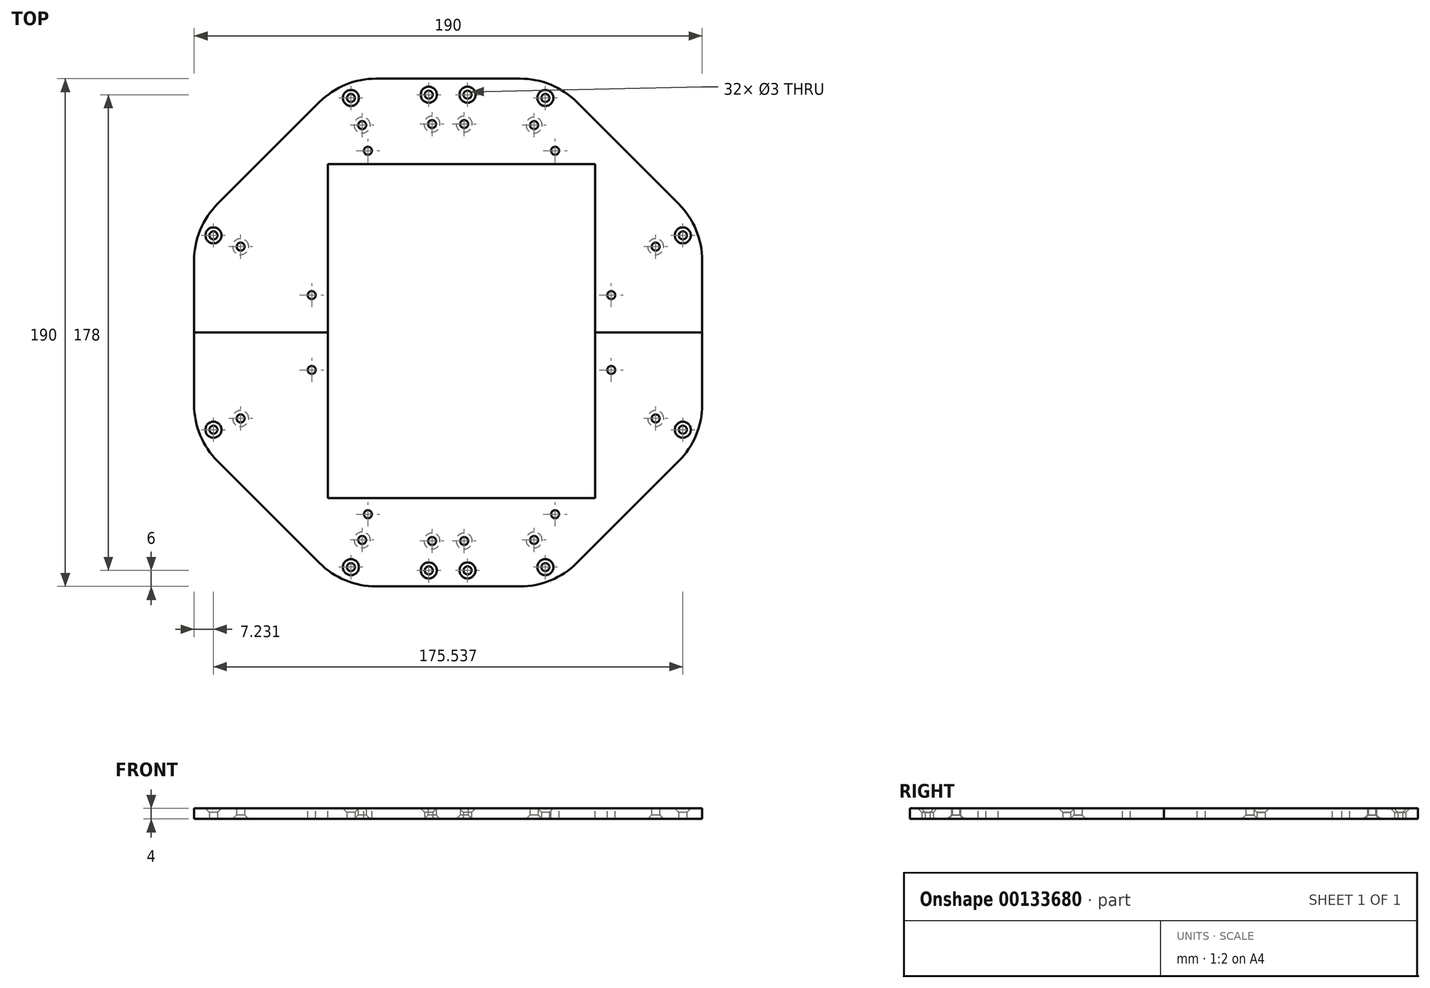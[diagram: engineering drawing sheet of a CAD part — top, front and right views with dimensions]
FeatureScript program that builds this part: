
annotation { "Feature Type Name" : "Feature", "Feature Type Description" : "" }
export const myFeature = defineFeature(function(context is Context, id is Id, definition is map)
    precondition{}
    {
        {
            var Q0;
            Q0=qCreatedBy(makeId("Top.planeOp"),FACE);
            var sketch = newSketch(context, id + "F0", { "sketchPlane" : qUnion([Q0])});
            skCircle(sketch, "E0.cCircle", {"center": v(0, 0) * mm, "radius": 95 * mm, "construction": true});
            skLineSegment(sketch, "E0.0", {"start": v(39.35, -95) * mm, "end": v(-39.35, -95) * mm});
            skLineSegment(sketch, "E0.1", {"start": v(-39.35, -95) * mm, "end": v(-95, -39.35) * mm});
            skLineSegment(sketch, "E0.2", {"start": v(-95, -39.35) * mm, "end": v(-95, 39.35) * mm});
            skLineSegment(sketch, "E0.3", {"start": v(-95, 39.35) * mm, "end": v(-39.35, 95) * mm});
            skLineSegment(sketch, "E0.4", {"start": v(-39.35, 95) * mm, "end": v(39.35, 95) * mm});
            skLineSegment(sketch, "E0.5", {"start": v(39.35, 95) * mm, "end": v(95, 39.35) * mm});
            skLineSegment(sketch, "E0.6", {"start": v(95, 39.35) * mm, "end": v(95, -39.35) * mm});
            skLineSegment(sketch, "E0.7", {"start": v(95, -39.35) * mm, "end": v(39.35, -95) * mm});
            skLineSegment(sketch, "E1", {"start": v(0, 0) * mm, "end": v(-95, 0) * mm});
            skLineSegment(sketch, "E2", {"start": v(0, 0) * mm, "end": v(95, 0) * mm});
            skLineSegment(sketch, "E3", {"start": v(-95, -39.35) * mm, "end": v(0, 0) * mm, "construction": true});
            skCircle(sketch, "E4", {"center": v(-87.77, -36.35) * mm, "radius": 1.5 * mm});
            skCircle(sketch, "E5.1.0", {"center": v(-36.35, -87.77) * mm, "radius": 1.5 * mm});
            skCircle(sketch, "E5.2.0", {"center": v(36.35, -87.77) * mm, "radius": 1.5 * mm});
            skCircle(sketch, "E5.3.0", {"center": v(87.77, -36.35) * mm, "radius": 1.5 * mm});
            skCircle(sketch, "E5.4.0", {"center": v(87.77, 36.35) * mm, "radius": 1.5 * mm});
            skCircle(sketch, "E5.5.0", {"center": v(36.35, 87.77) * mm, "radius": 1.5 * mm});
            skCircle(sketch, "E5.6.0", {"center": v(-36.35, 87.77) * mm, "radius": 1.5 * mm});
            skCircle(sketch, "E5.7.0", {"center": v(-87.77, 36.35) * mm, "radius": 1.5 * mm});
            skCircle(sketch, "E6", {"center": v(-77.6, -32.15) * mm, "radius": 1.5 * mm});
            skLineSegment(sketch, "E7", {"start": v(0, 0) * mm, "end": v(0, -89) * mm, "construction": true});
            skLineSegment(sketch, "E8", {"start": v(0, -89) * mm, "end": v(-7.25, -89) * mm, "construction": true});
            skLineSegment(sketch, "E9", {"start": v(0, -89) * mm, "end": v(7.25, -89) * mm, "construction": true});
            skCircle(sketch, "E10", {"center": v(-7.25, -89) * mm, "radius": 1.5 * mm});
            skCircle(sketch, "E11", {"center": v(7.25, -89) * mm, "radius": 1.5 * mm});
            skCircle(sketch, "E12.1.0", {"center": v(7.25, 89) * mm, "radius": 1.5 * mm});
            skCircle(sketch, "E12.1.1", {"center": v(-7.25, 89) * mm, "radius": 1.5 * mm});
            skCircle(sketch, "E13.1.0", {"center": v(-32.15, -77.6) * mm, "radius": 1.5 * mm});
            skCircle(sketch, "E13.2.0", {"center": v(32.15, -77.6) * mm, "radius": 1.5 * mm});
            skCircle(sketch, "E13.3.0", {"center": v(77.6, -32.15) * mm, "radius": 1.5 * mm});
            skCircle(sketch, "E13.4.0", {"center": v(77.6, 32.15) * mm, "radius": 1.5 * mm});
            skCircle(sketch, "E13.5.0", {"center": v(32.15, 77.6) * mm, "radius": 1.5 * mm});
            skCircle(sketch, "E13.6.0", {"center": v(-32.15, 77.6) * mm, "radius": 1.5 * mm});
            skCircle(sketch, "E13.7.0", {"center": v(-77.6, 32.15) * mm, "radius": 1.5 * mm});
            skLineSegment(sketch, "E14", {"start": v(0, -78) * mm, "end": v(-6, -78) * mm, "construction": true});
            skLineSegment(sketch, "E15", {"start": v(0, -78) * mm, "end": v(6, -78) * mm, "construction": true});
            skCircle(sketch, "E16", {"center": v(-6, -78) * mm, "radius": 1.5 * mm});
            skCircle(sketch, "E17", {"center": v(6, -78) * mm, "radius": 1.5 * mm});
            skCircle(sketch, "E18.1.0", {"center": v(-6, 78) * mm, "radius": 1.5 * mm});
            skCircle(sketch, "E18.1.1", {"center": v(6, 78) * mm, "radius": 1.5 * mm});
            skSolve(sketch);
        }
        {
            var Q0;
            {var subQ1=sQuery(id+"F0.wireOp",EDGE,"E0.3");Q0=makeQuery(id+"F0.imprint","IMPRINT",FACE,{"disambiguationData":[TD([[makeQuery(id+"F0.imprint","IMPRINT",EDGE,{"derivedFrom":subQ1}),-1.0]])]});}
            var Q1;
            {var subQ1=sQuery(id+"F0.wireOp",EDGE,"E0.3");Q1=makeQuery(id+"F0.imprint","IMPRINT",FACE,{"disambiguationData":[TD([[makeQuery(id+"F0.imprint","IMPRINT",EDGE,{"derivedFrom":subQ1}),-1.0]])]});}
            extrude(context, id + "F1", {"entities" : qUnion([Q0, Q1]), "depth" : 4 * mm});
        }
        {
            var Q0;
            Q0=makeQuery(id+"F0.imprint","IMPRINT",FACE,{"disambiguationData":[TD([[makeQuery(id+"F0.imprint","IMPRINT",EDGE,{"derivedFrom":sQuery(id+"F0.wireOp",EDGE,"E0.0")}),-1.0]])]});
            extrude(context, id + "F2", {"entities" : qUnion([Q0]), "depth" : 4 * mm});
        }
        {
            var Q0;
            Q0=makeQuery(id+"F2.opExtrude","SWEPT_EDGE",EDGE,{"disambiguationData":[OSD([sQuery(id+"F0.wireOp",EDGE,"E0.1"),sQuery(id+"F0.wireOp",EDGE,"E0.2")])]});
            var Q1;
            Q1=makeQuery(id+"F2.opExtrude","SWEPT_EDGE",EDGE,{"disambiguationData":[OSD([sQuery(id+"F0.wireOp",EDGE,"E0.6"),sQuery(id+"F0.wireOp",EDGE,"E0.7")])]});
            var Q2;
            Q2=makeQuery(id+"F1.opExtrude","SWEPT_EDGE",EDGE,{"disambiguationData":[OSD([sQuery(id+"F0.wireOp",EDGE,"E0.5"),sQuery(id+"F0.wireOp",EDGE,"E0.6")])]});
            var Q3;
            Q3=makeQuery(id+"F1.opExtrude","SWEPT_EDGE",EDGE,{"disambiguationData":[OSD([sQuery(id+"F0.wireOp",EDGE,"E0.4"),sQuery(id+"F0.wireOp",EDGE,"E0.5")])]});
            var Q4;
            Q4=makeQuery(id+"F1.opExtrude","SWEPT_EDGE",EDGE,{"disambiguationData":[OSD([sQuery(id+"F0.wireOp",EDGE,"E0.3"),sQuery(id+"F0.wireOp",EDGE,"E0.4")])]});
            var Q5;
            Q5=makeQuery(id+"F1.opExtrude","SWEPT_EDGE",EDGE,{"disambiguationData":[OSD([sQuery(id+"F0.wireOp",EDGE,"E0.2"),sQuery(id+"F0.wireOp",EDGE,"E0.3")])]});
            var Q6;
            Q6=makeQuery(id+"F2.opExtrude","SWEPT_EDGE",EDGE,{"disambiguationData":[OSD([sQuery(id+"F0.wireOp",EDGE,"E0.0"),sQuery(id+"F0.wireOp",EDGE,"E0.1")])]});
            var Q7;
            Q7=makeQuery(id+"F2.opExtrude","SWEPT_EDGE",EDGE,{"disambiguationData":[OSD([sQuery(id+"F0.wireOp",EDGE,"E0.0"),sQuery(id+"F0.wireOp",EDGE,"E0.7")])]});
            fillet(context, id + "F3", {"entities" : qUnion([Q0, Q1, Q2, Q3, Q4, Q5, Q6, Q7]), "radius" : 30 * mm, "tangentPropagation" : true, "allowEdgeOverflow" : false});
        }
        {
            var Q0;
            Q0=makeQuery(id+"F1.opExtrude","CAP_FACE",FACE,{"disambiguationData":[OSD([sQuery(id+"F0.wireOp",EDGE,"E0.2"),sQuery(id+"F0.wireOp",EDGE,"E0.3"),sQuery(id+"F0.wireOp",EDGE,"E0.4"),sQuery(id+"F0.wireOp",EDGE,"E0.5"),sQuery(id+"F0.wireOp",EDGE,"E0.6"),sQuery(id+"F0.wireOp",EDGE,"FWvXgzkW-92Ol-D1nR-HL31-QDwloOWlVPkl"),sQuery(id+"F0.wireOp",EDGE,"KB5lrl97-oh6M-4FKn-tIKZ-oEGIWaDHRA87"),sQuery(id+"F0.wireOp",EDGE,"1a06ab86-549c-4c23-92a1-abe76b86ff2b"),sQuery(id+"F0.wireOp",EDGE,"3b6d9c79-dd86-4e60-94f1-2d74a6fdfb3c.4.1"),sQuery(id+"F0.wireOp",EDGE,"3b6d9c79-dd86-4e60-94f1-2d74a6fdfb3c.5.0"),sQuery(id+"F0.wireOp",EDGE,"3b6d9c79-dd86-4e60-94f1-2d74a6fdfb3c.5.1"),sQuery(id+"F0.wireOp",EDGE,"3b6d9c79-dd86-4e60-94f1-2d74a6fdfb3c.6.0"),sQuery(id+"F0.wireOp",EDGE,"3b6d9c79-dd86-4e60-94f1-2d74a6fdfb3c.6.1"),sQuery(id+"F0.wireOp",EDGE,"3b6d9c79-dd86-4e60-94f1-2d74a6fdfb3c.7.0"),sQuery(id+"F0.wireOp",EDGE,"3b6d9c79-dd86-4e60-94f1-2d74a6fdfb3c.7.1")])],"isStart":false});
            var sketch = newSketch(context, id + "F4", { "sketchPlane" : qUnion([Q0])});
            skLineSegment(sketch, "E19.bottom", {"start": v(-30, 68) * mm, "end": v(40, 68) * mm, "construction": true});
            skLineSegment(sketch, "E19.top", {"start": v(-30, -68) * mm, "end": v(40, -68) * mm, "construction": true});
            skLineSegment(sketch, "E19.left", {"start": v(-30, 68) * mm, "end": v(-30, -68) * mm, "construction": true});
            skLineSegment(sketch, "E19.right", {"start": v(40, 68) * mm, "end": v(40, -68) * mm, "construction": true});
            skPoint(sketch, "E19.middle", {"position": v(0, 0) * mm});
            skCircle(sketch, "E20", {"center": v(-30, 68) * mm, "radius": 1.5 * mm});
            skCircle(sketch, "E21", {"center": v(40, 68) * mm, "radius": 1.5 * mm});
            skCircle(sketch, "E22", {"center": v(40, -68) * mm, "radius": 1.5 * mm});
            skCircle(sketch, "E23", {"center": v(-30, -68) * mm, "radius": 1.5 * mm});
            skPoint(sketch, "E24", {"position": v(5, 0) * mm});
            skPoint(sketch, "E24.positionSnap0", {"position": v(5, 68) * mm});
            skSolve(sketch);
        }
        {
            var Q0;
            Q0=makeQuery(id+"F4.imprint","IMPRINT",FACE,{"disambiguationData":[TD([[makeQuery(id+"F4.imprint","IMPRINT",EDGE,{"derivedFrom":sQuery(id+"F4.wireOp",EDGE,"E20")}),1.0]])]});
            var Q1;
            Q1=makeQuery(id+"F4.imprint","IMPRINT",FACE,{"disambiguationData":[TD([[makeQuery(id+"F4.imprint","IMPRINT",EDGE,{"derivedFrom":sQuery(id+"F4.wireOp",EDGE,"E21")}),1.0]])]});
            var Q2;
            Q2=makeQuery(id+"F4.imprint","IMPRINT",FACE,{"disambiguationData":[TD([[makeQuery(id+"F4.imprint","IMPRINT",EDGE,{"derivedFrom":sQuery(id+"F4.wireOp",EDGE,"E22")}),1.0]])]});
            var Q3;
            Q3=makeQuery(id+"F4.imprint","IMPRINT",FACE,{"disambiguationData":[TD([[makeQuery(id+"F4.imprint","IMPRINT",EDGE,{"derivedFrom":sQuery(id+"F4.wireOp",EDGE,"E23")}),1.0]])]});
            extrude(context, id + "F5", {"entities" : qUnion([Q0, Q1, Q2, Q3]), "operationType" : NewBodyOperationType.REMOVE, "oppositeDirection" : true, "depth" : 25 * mm});
        }
        {
            var Q0;
            Q0=makeQuery(id+"F1.opExtrude","CAP_FACE",FACE,{"disambiguationData":[OSD([sQuery(id+"F0.wireOp",EDGE,"E0.2"),sQuery(id+"F0.wireOp",EDGE,"E0.3"),sQuery(id+"F0.wireOp",EDGE,"E0.4"),sQuery(id+"F0.wireOp",EDGE,"E0.5"),sQuery(id+"F0.wireOp",EDGE,"E0.6"),sQuery(id+"F0.wireOp",EDGE,"FWvXgzkW-92Ol-D1nR-HL31-QDwloOWlVPkl"),sQuery(id+"F0.wireOp",EDGE,"KB5lrl97-oh6M-4FKn-tIKZ-oEGIWaDHRA87"),sQuery(id+"F0.wireOp",EDGE,"ce847c22-4656-4ac6-8dae-eb3496d83a06.7.0"),sQuery(id+"F0.wireOp",EDGE,"ce847c22-4656-4ac6-8dae-eb3496d83a06.7.1"),sQuery(id+"F0.wireOp",EDGE,"2ddf77b3-c7c5-494c-ac41-90231f072106.1.0"),sQuery(id+"F0.wireOp",EDGE,"2ddf77b3-c7c5-494c-ac41-90231f072106.1.1"),sQuery(id+"F0.wireOp",EDGE,"2ddf77b3-c7c5-494c-ac41-90231f072106.1.2"),sQuery(id+"F0.wireOp",EDGE,"2ddf77b3-c7c5-494c-ac41-90231f072106.1.3"),sQuery(id+"F0.wireOp",EDGE,"2ddf77b3-c7c5-494c-ac41-90231f072106.2.0"),sQuery(id+"F0.wireOp",EDGE,"2ddf77b3-c7c5-494c-ac41-90231f072106.2.1"),sQuery(id+"F0.wireOp",EDGE,"2ddf77b3-c7c5-494c-ac41-90231f072106.2.2"),sQuery(id+"F0.wireOp",EDGE,"2ddf77b3-c7c5-494c-ac41-90231f072106.2.3"),sQuery(id+"F0.wireOp",EDGE,"2ddf77b3-c7c5-494c-ac41-90231f072106.3.0"),sQuery(id+"F0.wireOp",EDGE,"2ddf77b3-c7c5-494c-ac41-90231f072106.3.1"),sQuery(id+"F0.wireOp",EDGE,"2ddf77b3-c7c5-494c-ac41-90231f072106.3.2"),sQuery(id+"F0.wireOp",EDGE,"2ddf77b3-c7c5-494c-ac41-90231f072106.3.3"),sQuery(id+"F0.wireOp",EDGE,"2ddf77b3-c7c5-494c-ac41-90231f072106.4.0"),sQuery(id+"F0.wireOp",EDGE,"2ddf77b3-c7c5-494c-ac41-90231f072106.4.1")])],"isStart":false});
            var sketch = newSketch(context, id + "F6", { "sketchPlane" : qUnion([Q0])});
            skLineSegment(sketch, "E25", {"start": v(-45, 63) * mm, "end": v(55, 63) * mm});
            skLineSegment(sketch, "E26", {"start": v(55, 63) * mm, "end": v(55, -62) * mm});
            skLineSegment(sketch, "E27.top", {"start": v(-45, -62) * mm, "end": v(55, -62) * mm});
            skLineSegment(sketch, "E27.left", {"start": v(-45, 63) * mm, "end": v(-45, -62) * mm});
            skLineSegment(sketch, "E28", {"start": v(-30, 68) * mm, "end": v(40, 68) * mm});
            skLineSegment(sketch, "E29", {"start": v(5, 68) * mm, "end": v(5, 63) * mm});
            skLineSegment(sketch, "E30", {"start": v(0, 0) * mm, "end": v(-51, 0) * mm});
            skLineSegment(sketch, "E31", {"start": v(-51, 0) * mm, "end": v(-51, -14) * mm});
            skLineSegment(sketch, "E32", {"start": v(-51, 0) * mm, "end": v(-51, 14) * mm});
            skCircle(sketch, "E33", {"center": v(-51, 14) * mm, "radius": 1.5 * mm});
            skCircle(sketch, "E34", {"center": v(-51, -14) * mm, "radius": 1.5 * mm});
            skLineSegment(sketch, "E35", {"start": v(0, 0) * mm, "end": v(61, 0) * mm});
            skLineSegment(sketch, "E36", {"start": v(61, 0) * mm, "end": v(61, 14) * mm});
            skLineSegment(sketch, "E37", {"start": v(61, 0) * mm, "end": v(61, -14) * mm});
            skCircle(sketch, "E38", {"center": v(61, 14) * mm, "radius": 1.5 * mm});
            skCircle(sketch, "E39", {"center": v(61, -14) * mm, "radius": 1.5 * mm});
            skLineSegment(sketch, "E40", {"start": v(61, 0) * mm, "end": v(0, 0) * mm});
            skSolve(sketch);
        }
        {
            var Q0;
            Q0=makeQuery(id+"F6.imprint","IMPRINT",FACE,{"disambiguationData":[TD([[makeQuery(id+"F6.imprint","IMPRINT",EDGE,{"derivedFrom":sQuery(id+"F6.wireOp",EDGE,"E33")}),1.0]])]});
            var Q1;
            Q1=makeQuery(id+"F6.imprint","IMPRINT",FACE,{"disambiguationData":[TD([[makeQuery(id+"F6.imprint","IMPRINT",EDGE,{"derivedFrom":sQuery(id+"F6.wireOp",EDGE,"E34")}),1.0]])]});
            var Q2;
            {var subQ5=sQuery(id+"F6.wireOp",EDGE,"E27.top");Q2=makeQuery(id+"F6.imprint","IMPRINT",FACE,{"disambiguationData":[TD([[makeQuery(id+"F6.imprint","IMPRINT",EDGE,{"derivedFrom":subQ5}),1.0]])]});}
            var Q3;
            {var subQ1=sQuery(id+"F6.wireOp",EDGE,"E25");var subQ5=makeQuery(id+"F6.imprint","IMPRINT",VERTEX,{"derivedFrom":subQ1});Q3=makeQuery(id+"F6.imprint","IMPRINT",FACE,{"disambiguationData":[TD([[makeQuery(id+"F6.imprint","IMPRINT",EDGE,{"disambiguationData":[TD([[subQ5,1.0]])],"derivedFrom":subQ1}),-1.0]])]});}
            var Q4;
            Q4=makeQuery(id+"F6.imprint","IMPRINT",FACE,{"disambiguationData":[TD([[makeQuery(id+"F6.imprint","IMPRINT",EDGE,{"derivedFrom":sQuery(id+"F6.wireOp",EDGE,"E38")}),1.0]])]});
            var Q5;
            Q5=makeQuery(id+"F6.imprint","IMPRINT",FACE,{"disambiguationData":[TD([[makeQuery(id+"F6.imprint","IMPRINT",EDGE,{"derivedFrom":sQuery(id+"F6.wireOp",EDGE,"E39")}),1.0]])]});
            extrude(context, id + "F7", {"entities" : qUnion([Q0, Q1, Q2, Q3, Q4, Q5]), "operationType" : NewBodyOperationType.REMOVE, "oppositeDirection" : true, "depth" : 25 * mm});
        }
        {
            var Q0;
            Q0=makeQuery(id+"F5.boolean.opBoolean","COPY",EDGE,{"derivedFrom":makeQuery(id+"F5.opExtrude","CAP_EDGE",EDGE,{"disambiguationData":[OSD([sQuery(id+"F4.wireOp",EDGE,"E20")])],"isStart":true})});
            var Q1;
            Q1=makeQuery(id+"F5.boolean.opBoolean","COPY",EDGE,{"derivedFrom":makeQuery(id+"F5.opExtrude","CAP_EDGE",EDGE,{"disambiguationData":[OSD([sQuery(id+"F4.wireOp",EDGE,"E21")])],"isStart":true})});
            var Q2;
            Q2=makeQuery(id+"F5.boolean.opBoolean","COPY",EDGE,{"derivedFrom":makeQuery(id+"F5.opExtrude","CAP_EDGE",EDGE,{"disambiguationData":[OSD([sQuery(id+"F4.wireOp",EDGE,"E23")])],"isStart":true})});
            var Q3;
            Q3=makeQuery(id+"F5.boolean.opBoolean","COPY",EDGE,{"derivedFrom":makeQuery(id+"F5.opExtrude","CAP_EDGE",EDGE,{"disambiguationData":[OSD([sQuery(id+"F4.wireOp",EDGE,"E22")])],"isStart":true})});
            var Q4;
            Q4=makeQuery(id+"F2.opExtrude","CAP_EDGE",EDGE,{"disambiguationData":[OSD([sQuery(id+"F0.wireOp",EDGE,"E5.2.0")])],"isStart":false});
            var Q5;
            Q5=makeQuery(id+"F2.opExtrude","CAP_EDGE",EDGE,{"disambiguationData":[OSD([sQuery(id+"F0.wireOp",EDGE,"E11")])],"isStart":false});
            var Q6;
            Q6=makeQuery(id+"F2.opExtrude","CAP_EDGE",EDGE,{"disambiguationData":[OSD([sQuery(id+"F0.wireOp",EDGE,"E10")])],"isStart":false});
            var Q7;
            Q7=makeQuery(id+"F2.opExtrude","CAP_EDGE",EDGE,{"disambiguationData":[OSD([sQuery(id+"F0.wireOp",EDGE,"E5.1.0")])],"isStart":false});
            var Q8;
            Q8=makeQuery(id+"F2.opExtrude","CAP_EDGE",EDGE,{"disambiguationData":[OSD([sQuery(id+"F0.wireOp",EDGE,"E4")])],"isStart":false});
            var Q9;
            Q9=makeQuery(id+"F1.opExtrude","CAP_EDGE",EDGE,{"disambiguationData":[OSD([sQuery(id+"F0.wireOp",EDGE,"E5.7.0")])],"isStart":false});
            var Q10;
            Q10=makeQuery(id+"F1.opExtrude","CAP_EDGE",EDGE,{"disambiguationData":[OSD([sQuery(id+"F0.wireOp",EDGE,"E5.6.0")])],"isStart":false});
            var Q11;
            Q11=makeQuery(id+"F1.opExtrude","CAP_EDGE",EDGE,{"disambiguationData":[OSD([sQuery(id+"F0.wireOp",EDGE,"E12.1.1")])],"isStart":false});
            var Q12;
            Q12=makeQuery(id+"F1.opExtrude","CAP_EDGE",EDGE,{"disambiguationData":[OSD([sQuery(id+"F0.wireOp",EDGE,"E12.1.0")])],"isStart":false});
            var Q13;
            Q13=makeQuery(id+"F1.opExtrude","CAP_EDGE",EDGE,{"disambiguationData":[OSD([sQuery(id+"F0.wireOp",EDGE,"E5.5.0")])],"isStart":false});
            var Q14;
            Q14=makeQuery(id+"F1.opExtrude","CAP_EDGE",EDGE,{"disambiguationData":[OSD([sQuery(id+"F0.wireOp",EDGE,"E5.4.0")])],"isStart":false});
            var Q15;
            Q15=makeQuery(id+"F2.opExtrude","CAP_EDGE",EDGE,{"disambiguationData":[OSD([sQuery(id+"F0.wireOp",EDGE,"E5.3.0")])],"isStart":false});
            var Q16;
            Q16=makeQuery(id+"F2.opExtrude","CAP_EDGE",EDGE,{"disambiguationData":[OSD([sQuery(id+"F0.wireOp",EDGE,"E6")])],"isStart":true});
            var Q17;
            Q17=makeQuery(id+"F2.opExtrude","CAP_EDGE",EDGE,{"disambiguationData":[OSD([sQuery(id+"F0.wireOp",EDGE,"E13.1.0")])],"isStart":true});
            var Q18;
            Q18=makeQuery(id+"F2.opExtrude","CAP_EDGE",EDGE,{"disambiguationData":[OSD([sQuery(id+"F0.wireOp",EDGE,"E16")])],"isStart":true});
            var Q19;
            Q19=makeQuery(id+"F2.opExtrude","CAP_EDGE",EDGE,{"disambiguationData":[OSD([sQuery(id+"F0.wireOp",EDGE,"E17")])],"isStart":true});
            var Q20;
            Q20=makeQuery(id+"F2.opExtrude","CAP_EDGE",EDGE,{"disambiguationData":[OSD([sQuery(id+"F0.wireOp",EDGE,"E13.2.0")])],"isStart":true});
            var Q21;
            Q21=makeQuery(id+"F2.opExtrude","CAP_EDGE",EDGE,{"disambiguationData":[OSD([sQuery(id+"F0.wireOp",EDGE,"E13.3.0")])],"isStart":true});
            var Q22;
            Q22=makeQuery(id+"F1.opExtrude","CAP_EDGE",EDGE,{"disambiguationData":[OSD([sQuery(id+"F0.wireOp",EDGE,"E13.7.0")])],"isStart":true});
            var Q23;
            Q23=makeQuery(id+"F1.opExtrude","CAP_EDGE",EDGE,{"disambiguationData":[OSD([sQuery(id+"F0.wireOp",EDGE,"E13.4.0")])],"isStart":true});
            var Q24;
            Q24=makeQuery(id+"F1.opExtrude","CAP_EDGE",EDGE,{"disambiguationData":[OSD([sQuery(id+"F0.wireOp",EDGE,"E13.5.0")])],"isStart":true});
            var Q25;
            Q25=makeQuery(id+"F1.opExtrude","CAP_EDGE",EDGE,{"disambiguationData":[OSD([sQuery(id+"F0.wireOp",EDGE,"E18.1.1")])],"isStart":true});
            var Q26;
            Q26=makeQuery(id+"F1.opExtrude","CAP_EDGE",EDGE,{"disambiguationData":[OSD([sQuery(id+"F0.wireOp",EDGE,"E18.1.0")])],"isStart":true});
            var Q27;
            Q27=makeQuery(id+"F1.opExtrude","CAP_EDGE",EDGE,{"disambiguationData":[OSD([sQuery(id+"F0.wireOp",EDGE,"E13.6.0")])],"isStart":true});
            var Q28;
            Q28=makeQuery(id+"F7.boolean.opBoolean","COPY",EDGE,{"derivedFrom":makeQuery(id+"F7.opExtrude","CAP_EDGE",EDGE,{"disambiguationData":[OSD([sQuery(id+"F6.wireOp",EDGE,"E33")])],"isStart":true})});
            var Q29;
            Q29=makeQuery(id+"F7.boolean.opBoolean","COPY",EDGE,{"derivedFrom":makeQuery(id+"F7.opExtrude","CAP_EDGE",EDGE,{"disambiguationData":[OSD([sQuery(id+"F6.wireOp",EDGE,"E34")])],"isStart":true})});
            var Q30;
            Q30=makeQuery(id+"F7.boolean.opBoolean","COPY",EDGE,{"derivedFrom":makeQuery(id+"F7.opExtrude","CAP_EDGE",EDGE,{"disambiguationData":[OSD([sQuery(id+"F6.wireOp",EDGE,"bf67a918-c99b-443f-873a-d6248eef8e750.MirrorC")])],"isStart":true})});
            var Q31;
            Q31=makeQuery(id+"F7.boolean.opBoolean","COPY",EDGE,{"derivedFrom":makeQuery(id+"F7.opExtrude","CAP_EDGE",EDGE,{"disambiguationData":[OSD([sQuery(id+"F6.wireOp",EDGE,"E38")])],"isStart":true})});
            var Q32;
            Q32=makeQuery(id+"F7.boolean.opBoolean","COPY",EDGE,{"derivedFrom":makeQuery(id+"F7.opExtrude","CAP_EDGE",EDGE,{"disambiguationData":[OSD([sQuery(id+"F6.wireOp",EDGE,"E39")])],"isStart":true})});
            chamfer(context, id + "F8", {"entities" : qUnion([Q0, Q1, Q2, Q3, Q4, Q5, Q6, Q7, Q8, Q9, Q10, Q11, Q12, Q13, Q14, Q15, Q16, Q17, Q18, Q19, Q20, Q21, Q22, Q23, Q24, Q25, Q26, Q27, Q28, Q29, Q30, Q31, Q32]), "width" : 1.5 * mm, "tangentPropagation" : true});
        }
    });
